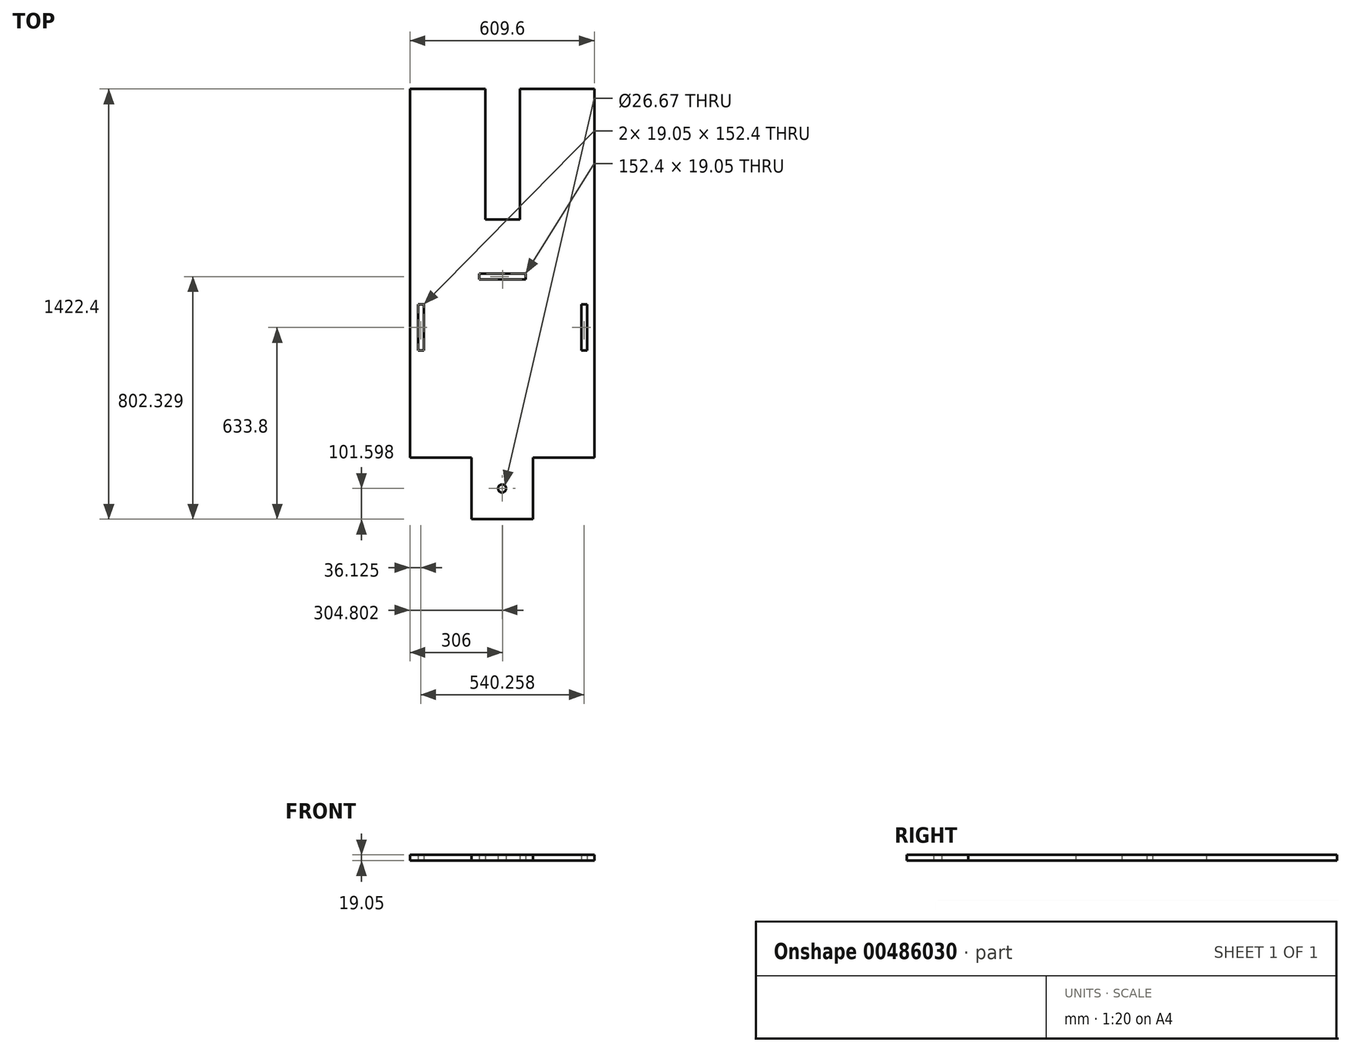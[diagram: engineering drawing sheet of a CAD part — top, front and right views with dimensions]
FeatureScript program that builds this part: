
annotation { "Feature Type Name" : "Feature", "Feature Type Description" : "" }
export const myFeature = defineFeature(function(context is Context, id is Id, definition is map)
    precondition{}
    {
        {
            var Q0;
            Q0=qCreatedBy(makeId("Top.planeOp"),FACE);
            var sketch = newSketch(context, id + "F0", { "sketchPlane" : qUnion([Q0])});
            skLineSegment(sketch, "E0.bottom", {"start": v(-306, -100.95) * mm, "end": v(303.6, -100.95) * mm});
            skLineSegment(sketch, "E0.top", {"start": v(-306, 1118.25) * mm, "end": v(303.6, 1118.25) * mm});
            skLineSegment(sketch, "E0.left", {"start": v(-306, -100.95) * mm, "end": v(-306, 1118.25) * mm});
            skLineSegment(sketch, "E0.right", {"start": v(303.6, -100.95) * mm, "end": v(303.6, 1118.25) * mm});
            skLineSegment(sketch, "E1", {"start": v(-306, -100.95) * mm, "end": v(-102.8, -100.95) * mm});
            skLineSegment(sketch, "E2", {"start": v(303.6, -100.95) * mm, "end": v(100.4, -100.95) * mm});
            skLineSegment(sketch, "E3", {"start": v(-102.8, -100.95) * mm, "end": v(-102.8, -304.15) * mm});
            skLineSegment(sketch, "E4", {"start": v(100.4, -100.95) * mm, "end": v(100.4, -304.15) * mm});
            skLineSegment(sketch, "E5", {"start": v(-102.8, -304.15) * mm, "end": v(100.4, -304.15) * mm});
            skCircle(sketch, "E6", {"center": v(-1.2, -202.55) * mm, "radius": 13.34 * mm});
            skLineSegment(sketch, "E7", {"start": v(0, 1118.25) * mm, "end": v(57.15, 1118.25) * mm});
            skLineSegment(sketch, "E8", {"start": v(0, 1118.25) * mm, "end": v(-57.15, 1118.25) * mm});
            skLineSegment(sketch, "E9.bottom", {"start": v(-57.15, 1118.25) * mm, "end": v(57.15, 1118.25) * mm});
            skLineSegment(sketch, "E9.top", {"start": v(-57.15, 686.45) * mm, "end": v(57.15, 686.45) * mm});
            skLineSegment(sketch, "E9.left", {"start": v(-57.15, 1118.25) * mm, "end": v(-57.15, 686.45) * mm});
            skLineSegment(sketch, "E9.right", {"start": v(57.15, 1118.25) * mm, "end": v(57.15, 686.45) * mm});
            skLineSegment(sketch, "E10", {"start": v(0, 498.18) * mm, "end": v(279.4, 498.18) * mm});
            skLineSegment(sketch, "E11", {"start": v(0, 498.18) * mm, "end": v(-279.4, 498.18) * mm});
            skLineSegment(sketch, "E12.bottom", {"start": v(76.2, 507.7) * mm, "end": v(-76.2, 507.7) * mm});
            skLineSegment(sketch, "E12.top", {"start": v(76.2, 488.65) * mm, "end": v(-76.2, 488.65) * mm});
            skLineSegment(sketch, "E12.left", {"start": v(76.2, 507.7) * mm, "end": v(76.2, 488.65) * mm});
            skLineSegment(sketch, "E12.right", {"start": v(-76.2, 507.7) * mm, "end": v(-76.2, 488.65) * mm});
            skPoint(sketch, "E12.middle", {"position": v(0, 498.18) * mm});
            skLineSegment(sketch, "E13", {"start": v(-279.4, 498.18) * mm, "end": v(-279.4, 405.85) * mm});
            skLineSegment(sketch, "E14.bottom", {"start": v(-279.4, 405.85) * mm, "end": v(-260.35, 405.85) * mm});
            skLineSegment(sketch, "E14.top", {"start": v(-279.4, 253.45) * mm, "end": v(-260.35, 253.45) * mm});
            skLineSegment(sketch, "E14.left", {"start": v(-279.4, 405.85) * mm, "end": v(-279.4, 253.45) * mm});
            skLineSegment(sketch, "E14.right", {"start": v(-260.35, 405.85) * mm, "end": v(-260.35, 253.45) * mm});
            skLineSegment(sketch, "E15.bottom", {"start": v(260.86, 405.85) * mm, "end": v(279.9, 405.85) * mm});
            skLineSegment(sketch, "E15.top", {"start": v(260.86, 253.45) * mm, "end": v(279.9, 253.45) * mm});
            skLineSegment(sketch, "E15.left", {"start": v(260.86, 405.85) * mm, "end": v(260.86, 253.45) * mm});
            skLineSegment(sketch, "E15.right", {"start": v(279.9, 405.85) * mm, "end": v(279.9, 253.45) * mm});
            skSolve(sketch);
        }
        {
            var Q0;
            Q0=makeQuery(id+"F0.imprint","IMPRINT",FACE,{"disambiguationData":[TD([[makeQuery(id+"F0.imprint","IMPRINT",EDGE,{"derivedFrom":sQuery(id+"F0.wireOp",EDGE,"E0.bottom")}),1.0]])]});
            var Q1;
            Q1=makeQuery(id+"F0.imprint","IMPRINT",FACE,{"disambiguationData":[TD([[makeQuery(id+"F0.imprint","IMPRINT",EDGE,{"derivedFrom":sQuery(id+"F0.wireOp",EDGE,"E0.bottom")}),-1.0]])]});
            extrude(context, id + "F1", {"entities" : qUnion([Q0, Q1]), "depth" : 19.05 * mm, "offsetDistance" : 25.4 * mm});
        }
    });
